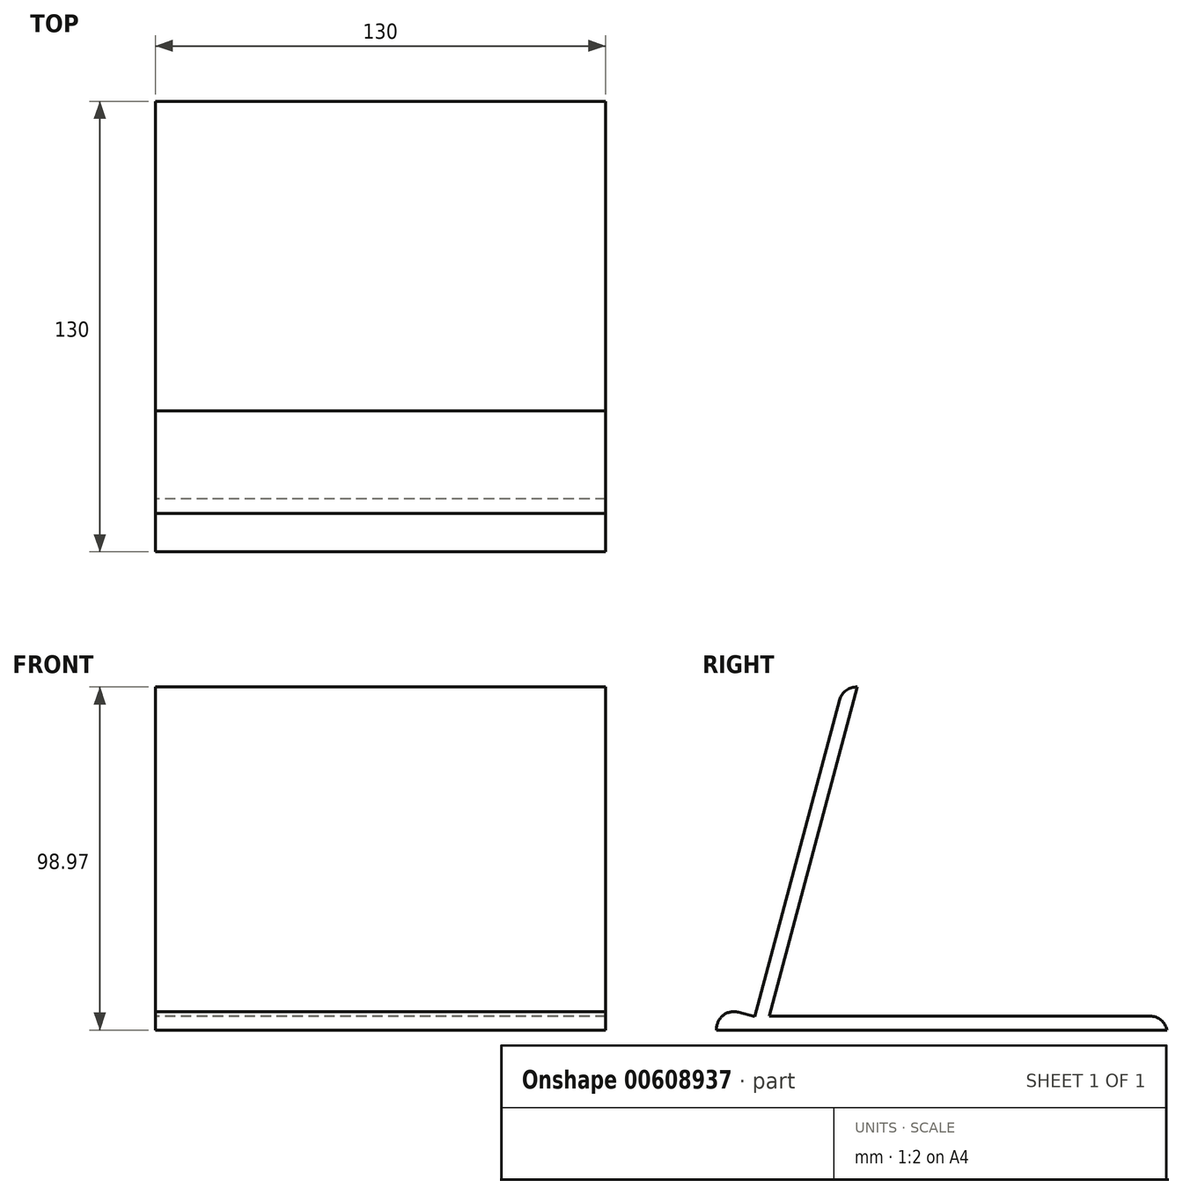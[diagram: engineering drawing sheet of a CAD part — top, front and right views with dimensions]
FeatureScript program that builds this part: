
annotation { "Feature Type Name" : "Feature", "Feature Type Description" : "" }
export const myFeature = defineFeature(function(context is Context, id is Id, definition is map)
    precondition{}
    {
        {
            var Q0;
            Q0=qCreatedBy(makeId("Right.planeOp"),FACE);
            var sketch = newSketch(context, id + "F0", { "sketchPlane" : qUnion([Q0])});
            skLineSegment(sketch, "E0", {"start": v(0, 0) * mm, "end": v(120, 0) * mm});
            skLineSegment(sketch, "E1", {"start": v(120, 0) * mm, "end": v(120, 4) * mm});
            skLineSegment(sketch, "E2", {"start": v(120, 4) * mm, "end": v(5.21, 4) * mm});
            skLineSegment(sketch, "E3", {"start": v(5.21, 4) * mm, "end": v(30.66, 98.96) * mm});
            skLineSegment(sketch, "E4", {"start": v(30.66, 98.96) * mm, "end": v(26.8, 100) * mm});
            skLineSegment(sketch, "E5", {"start": v(26.8, 100) * mm, "end": v(0, 0) * mm});
            skLineSegment(sketch, "E6", {"start": v(0, 0) * mm, "end": v(-10, 0) * mm});
            skLineSegment(sketch, "E7", {"start": v(-10, 0) * mm, "end": v(-10, 4) * mm});
            skLineSegment(sketch, "E8", {"start": v(1.04, 3.86) * mm, "end": v(-10, 6.82) * mm});
            skLineSegment(sketch, "E9", {"start": v(-10, 6.82) * mm, "end": v(-10, 4) * mm});
            skLineSegment(sketch, "E10", {"start": v(1.04, 3.86) * mm, "end": v(0, 0) * mm});
            skSolve(sketch);
        }
        {
            var Q0;
            Q0 = qSketchRegion(id + "F0", true);
            extrude(context, id + "F1", {"entities" : qUnion([Q0]), "depth" : 130 * mm, "offsetDistance" : 25 * mm});
        }
        {
            var Q0;
            Q0=makeQuery(id+"F1.opExtrude","SWEPT_EDGE",EDGE,{"disambiguationData":[OSD([sQuery(id+"F0.wireOp",EDGE,"E4"),sQuery(id+"F0.wireOp",EDGE,"E5")])]});
            fillet(context, id + "F2", {"entities" : qUnion([Q0]), "radius" : 5 * mm, "tangentPropagation" : true, "allowEdgeOverflow" : false});
        }
        {
            var Q0;
            Q0=makeQuery(id+"F1.opExtrude","SWEPT_EDGE",EDGE,{"disambiguationData":[OSD([sQuery(id+"F0.wireOp",EDGE,"E1"),sQuery(id+"F0.wireOp",EDGE,"E2")])]});
            fillet(context, id + "F3", {"entities" : qUnion([Q0]), "radius" : 5 * mm, "tangentPropagation" : true, "allowEdgeOverflow" : false});
        }
        {
            var Q0;
            Q0=makeQuery(id+"F1.opExtrude","SWEPT_EDGE",EDGE,{"disambiguationData":[OSD([sQuery(id+"F0.wireOp",EDGE,"E8"),sQuery(id+"F0.wireOp",EDGE,"E9")])]});
            fillet(context, id + "F4", {"entities" : qUnion([Q0]), "radius" : 5 * mm, "tangentPropagation" : true, "allowEdgeOverflow" : false});
        }
    });
